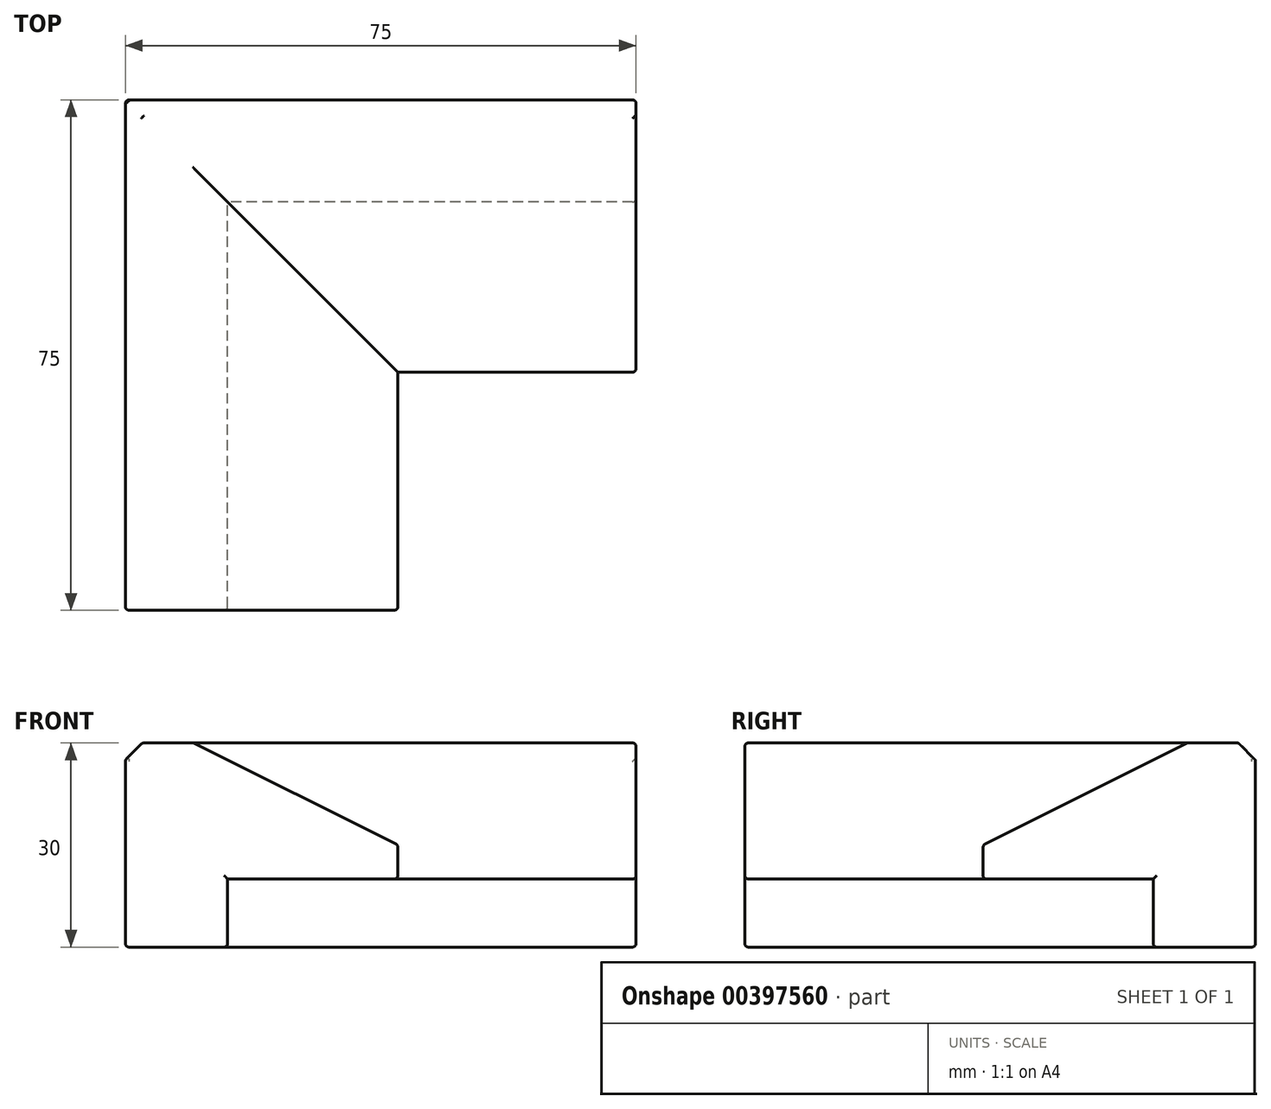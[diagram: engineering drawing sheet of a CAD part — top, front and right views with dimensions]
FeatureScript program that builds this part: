
annotation { "Feature Type Name" : "Feature", "Feature Type Description" : "" }
export const myFeature = defineFeature(function(context is Context, id is Id, definition is map)
    precondition{}
    {
        {
            var Q0;
            Q0=qCreatedBy(makeId("Right.planeOp"),FACE);
            var sketch = newSketch(context, id + "F0", { "sketchPlane" : qUnion([Q0])});
            skLineSegment(sketch, "E0.bottom", {"start": v(20, 15) * mm, "end": v(-20, 15) * mm});
            skLineSegment(sketch, "E0.top", {"start": v(20, -15) * mm, "end": v(-20, -15) * mm});
            skLineSegment(sketch, "E0.left", {"start": v(20, 15) * mm, "end": v(20, -15) * mm});
            skLineSegment(sketch, "E0.right", {"start": v(-20, 15) * mm, "end": v(-20, -15) * mm});
            skPoint(sketch, "E0.middle", {"position": v(0, 0) * mm});
            skLineSegment(sketch, "E1", {"start": v(-20, -5) * mm, "end": v(5, -5) * mm});
            skLineSegment(sketch, "E2", {"start": v(5, -5) * mm, "end": v(5, -15) * mm});
            skLineSegment(sketch, "E3", {"start": v(-20, 0) * mm, "end": v(10, 15) * mm});
            skSolve(sketch);
        }
        {
            var Q0;
            {var subQ3=sQuery(id+"F0.wireOp",EDGE,"E0.left");Q0=makeQuery(id+"F0.imprint","IMPRINT",FACE,{"disambiguationData":[TD([[makeQuery(id+"F0.imprint","IMPRINT",EDGE,{"derivedFrom":subQ3}),-1.0]])]});}
            extrude(context, id + "F1", {"entities" : qUnion([Q0]), "depth" : 75 * mm});
        }
        {
            var Q0;
            Q0=makeQuery(id+"F1.opExtrude","SWEPT_FACE",FACE,{"disambiguationData":[OSD([sQuery(id+"F0.wireOp",EDGE,"E0.bottom")])]});
            var sketch = newSketch(context, id + "F2", { "sketchPlane" : qUnion([Q0])});
            skPoint(sketch, "E4.0", {"position": v(0, 20) * mm});
            skLineSegment(sketch, "E4.1", {"start": v(75, -20) * mm, "end": v(0, -20) * mm});
            skLineSegment(sketch, "E5", {"start": v(0, 20) * mm, "end": v(40, -20) * mm});
            skLineSegment(sketch, "E6.0", {"start": v(75, 20) * mm, "end": v(0, 20) * mm, "construction": true});
            skLineSegment(sketch, "E7", {"start": v(40, -20) * mm, "end": v(40, 20) * mm, "construction": true});
            skLineSegment(sketch, "E8", {"start": v(40, -20) * mm, "end": v(0, -20) * mm, "construction": true});
            skLineSegment(sketch, "E9", {"start": v(0, 20) * mm, "end": v(0, -20) * mm});
            skSolve(sketch);
        }
        {
            var Q0;
            {var subQ1=sQuery(id+"F2.wireOp",EDGE,"E5");var subQ2=sQuery(id+"F0.wireOp",EDGE,"E0.bottom");var subQ4=makeQuery(id+"F1.opExtrude","SWEPT_EDGE",EDGE,{"disambiguationData":[OSD([subQ2,sQuery(id+"F0.wireOp",EDGE,"E3")])]});var subQ5=makeQuery(id+"F2.imprint","INTERSECT",VERTEX,{"derivedFrom":[subQ4,subQ1]});Q0=makeQuery(id+"F2.imprint","IMPRINT",FACE,{"disambiguationData":[TD([[makeQuery(id+"F2.imprint","IMPRINT",EDGE,{"disambiguationData":[TD([[subQ5,1.0]])],"derivedFrom":subQ1}),-1.0]])]});}
            var Q1;
            {var subQ0=sQuery(id+"F2.wireOp",EDGE,"E9");var subQ1=sQuery(id+"F2.wireOp",EDGE,"E4.1");var subQ2=makeQuery(id+"F2.imprint","INTERSECT",VERTEX,{"derivedFrom":[subQ1,subQ0]});Q1=makeQuery(id+"F2.imprint","IMPRINT",FACE,{"disambiguationData":[TD([[makeQuery(id+"F2.imprint","IMPRINT",EDGE,{"disambiguationData":[TD([[subQ2,1.0]])],"derivedFrom":subQ1}),-1.0]])]});}
            var Q2;
            Q2=makeQuery(id+"F1.opExtrude","SWEPT_FACE",FACE,{"disambiguationData":[OSD([sQuery(id+"F0.wireOp",EDGE,"E0.top")])]});
            extrude(context, id + "F3", {"entities" : qUnion([Q0, Q1]), "operationType" : NewBodyOperationType.REMOVE, "endBound" : BoundingType.UP_TO_SURFACE, "oppositeDirection" : true, "endBoundEntityFace" : qUnion([Q2]), "depth" : 25 * mm});
        }
        {
            var Q0;
            Q0=makeQuery(id+"F1.opExtrude","SWEPT_FACE",FACE,{"disambiguationData":[OSD([sQuery(id+"F0.wireOp",EDGE,"E0.left")])]});
            var sketch = newSketch(context, id + "F4", { "sketchPlane" : qUnion([Q0])});
            skPoint(sketch, "E10.0", {"position": v(0, -15) * mm});
            skPoint(sketch, "E10.1", {"position": v(0, 15) * mm});
            skPoint(sketch, "E10.2", {"position": v(-10, 15) * mm});
            skPoint(sketch, "E10.3", {"position": v(-40, 0) * mm});
            skPoint(sketch, "E10.4", {"position": v(-40, -5) * mm});
            skPoint(sketch, "E10.5", {"position": v(-15, -5) * mm});
            skPoint(sketch, "E10.6", {"position": v(-15, -15) * mm});
            skLineSegment(sketch, "E11", {"start": v(-15, -15) * mm, "end": v(-15, -5) * mm});
            skLineSegment(sketch, "E12", {"start": v(-40, -5) * mm, "end": v(-15, -5) * mm});
            skLineSegment(sketch, "E13", {"start": v(-40, -5) * mm, "end": v(-40, 0) * mm});
            skLineSegment(sketch, "E14", {"start": v(-40, 0) * mm, "end": v(-10, 15) * mm});
            skSolve(sketch);
        }
        {
            var Q0;
            {var subQ1=sQuery(id+"F4.wireOp",EDGE,"E11");Q0=makeQuery(id+"F4.imprint","IMPRINT",FACE,{"disambiguationData":[TD([[makeQuery(id+"F4.imprint","IMPRINT",EDGE,{"derivedFrom":subQ1}),-1.0]])]});}
            extrude(context, id + "F5", {"entities" : qUnion([Q0]), "operationType" : NewBodyOperationType.ADD, "oppositeDirection" : true, "depth" : 75 * mm});
        }
        {
            var Q0;
            Q0=makeQuery(id+"F1.opExtrude","SWEPT_EDGE",EDGE,{"disambiguationData":[OSD([sQuery(id+"F0.wireOp",EDGE,"E0.bottom"),sQuery(id+"F0.wireOp",EDGE,"E0.left")])]});
            var Q1;
            Q1=makeQuery(id+"F5.opExtrude","SWEPT_EDGE",EDGE,{"disambiguationData":[OSD([sQuery(id+"F0.wireOp",EDGE,"E0.bottom"),sQuery(id+"F0.wireOp",EDGE,"E0.left"),sQuery(id+"F2.wireOp",EDGE,"E5"),sQuery(id+"F2.wireOp",EDGE,"E9")])]});
            chamfer(context, id + "F6", {"entities" : qUnion([Q0, Q1]), "width" : 2.5 * mm, "tangentPropagation" : true});
        }
        {
            var Q0;
            {var subQ0=sQuery(id+"F0.wireOp",EDGE,"E0.bottom");Q0=makeQuery(id+"F5.boolean.opBoolean","MERGE",FACE,{"derivedFrom":[makeQuery(id+"F1.opExtrude","SWEPT_FACE",FACE,{"disambiguationData":[OSD([subQ0])]}),makeQuery(id+"F5.opExtrude","SWEPT_FACE",FACE,{"disambiguationData":[OSD([subQ0,sQuery(id+"F0.wireOp",EDGE,"E0.left")])]})]});}
            var Q1;
            {var subQ0=sQuery(id+"F0.wireOp",EDGE,"E0.left");var subQ1=sQuery(id+"F0.wireOp",EDGE,"E0.bottom");Q1=makeQuery(id+"F6.opChamfer","BLEND_EDGE",EDGE,{"blendedFrom":[makeQuery(id+"F5.opExtrude","SWEPT_EDGE",EDGE,{"disambiguationData":[OSD([subQ1,subQ0,sQuery(id+"F2.wireOp",EDGE,"E5"),sQuery(id+"F2.wireOp",EDGE,"E9")])]}),makeQuery(id+"F1.opExtrude","SWEPT_EDGE",EDGE,{"disambiguationData":[OSD([subQ1,subQ0])]})],"blendedInto":[]});}
            var Q2;
            {var subQ0=sQuery(id+"F2.wireOp",EDGE,"E9");var subQ1=sQuery(id+"F2.wireOp",EDGE,"E5");var subQ2=sQuery(id+"F0.wireOp",EDGE,"E0.left");var subQ3=sQuery(id+"F0.wireOp",EDGE,"E0.bottom");Q2=makeQuery(id+"F6.opChamfer","BLEND_EDGE",EDGE,{"blendedFrom":[makeQuery(id+"F5.opExtrude","SWEPT_EDGE",EDGE,{"disambiguationData":[OSD([subQ3,subQ2,subQ1,subQ0])]}),makeQuery(id+"F5.opExtrude","SWEPT_FACE",FACE,{"disambiguationData":[OSD([subQ3,subQ2,subQ1,subQ0])]})],"blendedInto":[makeQuery(id+"F5.opExtrude","SWEPT_FACE",FACE,{"disambiguationData":[OSD([subQ3,subQ2,subQ1,subQ0])]})]});}
            var Q3;
            {var subQ0=sQuery(id+"F0.wireOp",EDGE,"E0.left");Q3=makeQuery(id+"F6.opChamfer","BLEND_EDGE",EDGE,{"blendedFrom":[makeQuery(id+"F1.opExtrude","SWEPT_EDGE",EDGE,{"disambiguationData":[OSD([sQuery(id+"F0.wireOp",EDGE,"E0.bottom"),subQ0])]}),makeQuery(id+"F1.opExtrude","SWEPT_FACE",FACE,{"disambiguationData":[OSD([subQ0])]})],"blendedInto":[makeQuery(id+"F1.opExtrude","SWEPT_FACE",FACE,{"disambiguationData":[OSD([subQ0])]})]});}
            var Q4;
            Q4=makeQuery(id+"F1.opExtrude","SWEPT_FACE",FACE,{"disambiguationData":[OSD([sQuery(id+"F0.wireOp",EDGE,"E0.left")])]});
            var Q5;
            {var subQ0=sQuery(id+"F2.wireOp",EDGE,"E9");var subQ1=sQuery(id+"F2.wireOp",EDGE,"E5");var subQ2=sQuery(id+"F0.wireOp",EDGE,"E0.left");var subQ3=sQuery(id+"F0.wireOp",EDGE,"E0.bottom");Q5=makeQuery(id+"F5.boolean.opBoolean","MERGE",EDGE,{"derivedFrom":[makeQuery(id+"F3.boolean.opBoolean","MERGE",EDGE,{"derivedFrom":[makeQuery(id+"F1.opExtrude","CAP_EDGE",EDGE,{"disambiguationData":[OSD([subQ2])],"isStart":true}),makeQuery(id+"F3.opExtrude","SWEPT_EDGE",EDGE,{"disambiguationData":[OSD([subQ3,subQ2,subQ1,subQ0])]})]}),makeQuery(id+"F5.opExtrude","CAP_EDGE",EDGE,{"disambiguationData":[OSD([subQ3,subQ2,subQ1,subQ0])],"isStart":true})]});}
            var Q6;
            Q6=makeQuery(id+"F1.opExtrude","SWEPT_EDGE",EDGE,{"disambiguationData":[OSD([sQuery(id+"F0.wireOp",EDGE,"E0.top"),sQuery(id+"F0.wireOp",EDGE,"E0.left")])]});
            var Q7;
            Q7=makeQuery(id+"F5.opExtrude","SWEPT_EDGE",EDGE,{"disambiguationData":[OSD([sQuery(id+"F0.wireOp",EDGE,"E0.bottom"),sQuery(id+"F0.wireOp",EDGE,"E0.top"),sQuery(id+"F0.wireOp",EDGE,"E0.left"),sQuery(id+"F2.wireOp",EDGE,"E5"),sQuery(id+"F2.wireOp",EDGE,"E9")])]});
            var Q8;
            Q8=makeQuery(id+"F5.opExtrude","CAP_EDGE",EDGE,{"disambiguationData":[OSD([sQuery(id+"F0.wireOp",EDGE,"E0.bottom"),sQuery(id+"F0.wireOp",EDGE,"E0.left"),sQuery(id+"F2.wireOp",EDGE,"E5"),sQuery(id+"F2.wireOp",EDGE,"E9")])],"isStart":false});
            var Q9;
            {var subQ0=sQuery(id+"F2.wireOp",EDGE,"E9");var subQ1=sQuery(id+"F2.wireOp",EDGE,"E5");var subQ2=sQuery(id+"F0.wireOp",EDGE,"E0.left");var subQ3=sQuery(id+"F0.wireOp",EDGE,"E0.bottom");Q9=makeQuery(id+"F6.opChamfer","BLEND_EDGE",EDGE,{"blendedFrom":[makeQuery(id+"F5.opExtrude","SWEPT_EDGE",EDGE,{"disambiguationData":[OSD([subQ3,subQ2,subQ1,subQ0])]}),makeQuery(id+"F5.opExtrude","CAP_FACE",FACE,{"disambiguationData":[OSD([subQ3,sQuery(id+"F0.wireOp",EDGE,"E0.top"),subQ2,subQ1,subQ0,sQuery(id+"F4.wireOp",EDGE,"E11"),sQuery(id+"F4.wireOp",EDGE,"E12"),sQuery(id+"F4.wireOp",EDGE,"E13"),sQuery(id+"F4.wireOp",EDGE,"E14")])],"isStart":false})],"blendedInto":[makeQuery(id+"F5.opExtrude","CAP_FACE",FACE,{"disambiguationData":[OSD([subQ3,sQuery(id+"F0.wireOp",EDGE,"E0.top"),subQ2,subQ1,subQ0,sQuery(id+"F4.wireOp",EDGE,"E11"),sQuery(id+"F4.wireOp",EDGE,"E12"),sQuery(id+"F4.wireOp",EDGE,"E13"),sQuery(id+"F4.wireOp",EDGE,"E14")])],"isStart":false})]});}
            var Q10;
            Q10=makeQuery(id+"F1.opExtrude","CAP_EDGE",EDGE,{"disambiguationData":[OSD([sQuery(id+"F0.wireOp",EDGE,"E3")])],"isStart":false});
            var Q11;
            Q11=makeQuery(id+"F5.opExtrude","CAP_EDGE",EDGE,{"disambiguationData":[OSD([sQuery(id+"F4.wireOp",EDGE,"E14")])],"isStart":false});
            var Q12;
            Q12=makeQuery(id+"F5.opExtrude","CAP_EDGE",EDGE,{"disambiguationData":[OSD([sQuery(id+"F0.wireOp",EDGE,"E0.top"),sQuery(id+"F0.wireOp",EDGE,"E0.left")])],"isStart":false});
            var Q13;
            Q13=makeQuery(id+"F5.opExtrude","CAP_EDGE",EDGE,{"disambiguationData":[OSD([sQuery(id+"F4.wireOp",EDGE,"E12")])],"isStart":false});
            var Q14;
            Q14=makeQuery(id+"F5.opExtrude","CAP_EDGE",EDGE,{"disambiguationData":[OSD([sQuery(id+"F4.wireOp",EDGE,"E13")])],"isStart":false});
            var Q15;
            Q15=makeQuery(id+"F1.opExtrude","CAP_EDGE",EDGE,{"disambiguationData":[OSD([sQuery(id+"F0.wireOp",EDGE,"E0.right")])],"isStart":false});
            var Q16;
            Q16=makeQuery(id+"F1.opExtrude","CAP_EDGE",EDGE,{"disambiguationData":[OSD([sQuery(id+"F0.wireOp",EDGE,"E1")])],"isStart":false});
            var Q17;
            Q17=makeQuery(id+"F1.opExtrude","CAP_EDGE",EDGE,{"disambiguationData":[OSD([sQuery(id+"F0.wireOp",EDGE,"E2")])],"isStart":false});
            var Q18;
            Q18=makeQuery(id+"F1.opExtrude","CAP_EDGE",EDGE,{"disambiguationData":[OSD([sQuery(id+"F0.wireOp",EDGE,"E0.top")])],"isStart":false});
            var Q19;
            Q19=makeQuery(id+"F5.opExtrude","SWEPT_EDGE",EDGE,{"disambiguationData":[OSD([sQuery(id+"F4.wireOp",EDGE,"E13"),sQuery(id+"F4.wireOp",EDGE,"E14")])]});
            var Q20;
            Q20=makeQuery(id+"F1.opExtrude","SWEPT_EDGE",EDGE,{"disambiguationData":[OSD([sQuery(id+"F0.wireOp",EDGE,"E0.right"),sQuery(id+"F0.wireOp",EDGE,"E3")])]});
            var Q21;
            Q21=makeQuery(id+"F1.opExtrude","SWEPT_EDGE",EDGE,{"disambiguationData":[OSD([sQuery(id+"F0.wireOp",EDGE,"E0.right"),sQuery(id+"F0.wireOp",EDGE,"E1")])]});
            var Q22;
            Q22=makeQuery(id+"F5.opExtrude","SWEPT_EDGE",EDGE,{"disambiguationData":[OSD([sQuery(id+"F4.wireOp",EDGE,"E12"),sQuery(id+"F4.wireOp",EDGE,"E13")])]});
            var Q23;
            Q23=makeQuery(id+"F5.opExtrude","CAP_EDGE",EDGE,{"disambiguationData":[OSD([sQuery(id+"F4.wireOp",EDGE,"E11")])],"isStart":false});
            var Q24;
            Q24=makeQuery(id+"F5.opExtrude","SWEPT_EDGE",EDGE,{"disambiguationData":[OSD([sQuery(id+"F0.wireOp",EDGE,"E0.top"),sQuery(id+"F0.wireOp",EDGE,"E0.left"),sQuery(id+"F4.wireOp",EDGE,"E11")])]});
            var Q25;
            Q25=makeQuery(id+"F1.opExtrude","SWEPT_EDGE",EDGE,{"disambiguationData":[OSD([sQuery(id+"F0.wireOp",EDGE,"E0.top"),sQuery(id+"F0.wireOp",EDGE,"E2")])]});
            fillet(context, id + "F7", {"entities" : qUnion([Q0, Q1, Q2, Q3, Q4, Q5, Q6, Q7, Q8, Q9, Q10, Q11, Q12, Q13, Q14, Q15, Q16, Q17, Q18, Q19, Q20, Q21, Q22, Q23, Q24, Q25]), "radius" : .5 * mm, "tangentPropagation" : true, "allowEdgeOverflow" : false});
        }
    });
